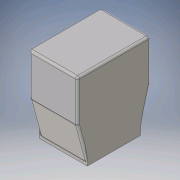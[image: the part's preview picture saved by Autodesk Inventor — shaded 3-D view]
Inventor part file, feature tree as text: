
AUTODESK INVENTOR PART (.ipt)
format: ipt  version: 2016 (Build 200138000, 138)  size: 190,976 bytes
history: native  units: in
note: dims shown in document units (in); Inventor stores cm internally (conversion verified against a paired STEP export)
features: sketch x4, extrude x3, hole x1, plane x1, fillet x1
ambient origin geometry x8: Origin, YZ Plane, XZ Plane, XY Plane, X Axis, Y Axis, Z Axis, Center Point
bodies: Solid1 (feature_tree)
feature tree (10):
  extrude  "Extrusion1"  Depth=2.0079in
  hole  "Hole1"  [1 undecoded]
  plane  "Work Plane1"
  extrude  "Extrusion3"  Depth=0.315in
  extrude  "Extrusion4"  Depth=0.0787in
  fillet  "Fillet1"  Radius=0.315in
  sketch  "Sketch1"  dims[d0=1.811in d1=2.0079in]
  sketch  "Sketch2"  dims[d2=0.1181in d3=0.0in d4=0.315in]
  sketch  "Sketch3"  dims[d5=0.315in d6=0.315in]
  sketch  "Sketch4"  dims[d7=0.315in d8=0.315in d9=0.315in d10=0.315in d11=0.315in d12=0.0787in d13=0.2362in d14=0.1575in d15=0.0787in d16=90.0deg d17=0.315in d18=0.8108in d19=7.874in d20=2.7559in d23=1.5748in d24=1.5748in d25=0.1181in d26=0.0in d27=0.1181in d28=0.1181in d29=0.1181in d30=0.1181in d31=0.1181in d32=1.6929in d33=0.0in d34=0.0787in]
note: 1 required parameter value undecoded (feature->parameter linkage not recoverable at this tier; creation-order binding heuristic only, values carry confidence <= 0.55)
